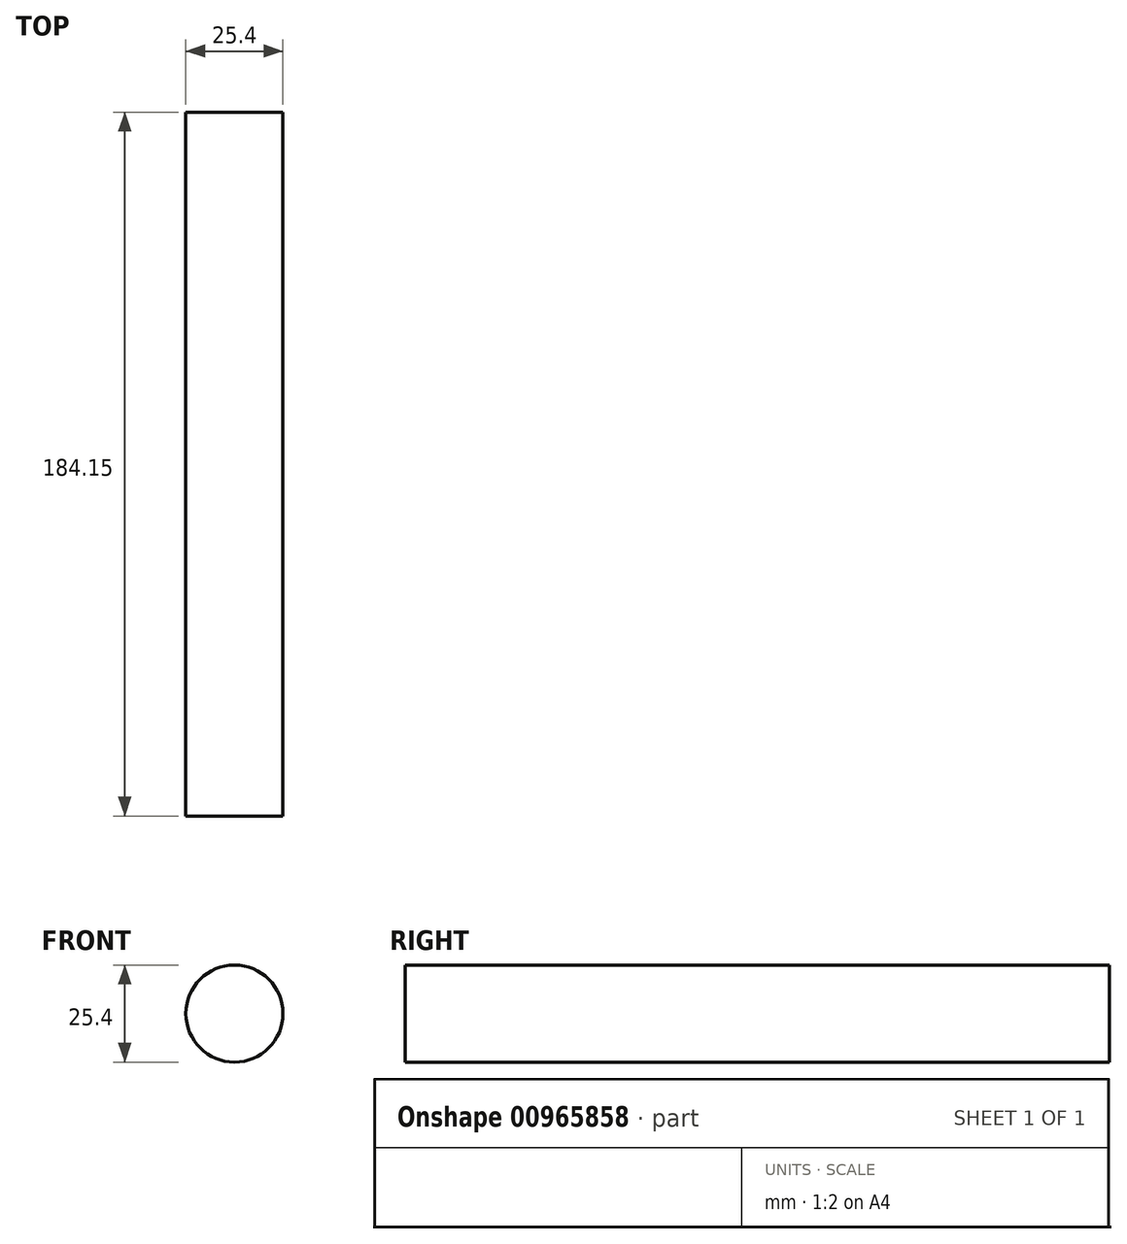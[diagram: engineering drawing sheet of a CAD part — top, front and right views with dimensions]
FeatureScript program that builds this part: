
annotation { "Feature Type Name" : "Feature", "Feature Type Description" : "" }
export const myFeature = defineFeature(function(context is Context, id is Id, definition is map)
    precondition{}
    {
        {
            var Q0;
            Q0=qCreatedBy(makeId("Front.planeOp"),FACE);
            var sketch = newSketch(context, id + "F0", { "sketchPlane" : qUnion([Q0])});
            skCircle(sketch, "E0", {"center": v(0, 0) * mm, "radius": 12.7 * mm});
            skSolve(sketch);
        }
        {
            var Q0;
            Q0 = qSketchRegion(id + "F0", true);
            extrude(context, id + "F1", {"entities" : qUnion([Q0]), "depth" : 184.15 * mm, "offsetDistance" : 25.4 * mm});
        }
    });
